# Revit family: RRPOSTM
name_source: partatom
category: Generic Models
revit_build: Autodesk Revit 2018 (Build: 20190510_1515(x64)
units: mm (PartAtom-declared; Revit-internal decimal feet)

## family parameters
Always vertical = No
Can host rebar = No
Cut with Voids When Loaded = No
Part Type = Normal
Room Calculation Point = No
Round Connector Dimension = Use Diameter
Shared = Yes
Work Plane-Based = Yes

## types (8) — shared parameters
Cap Height = 1.5 "
Default Elevation = 48 "
Diameter = 2.38 "
Patent Information = 10495237, 10,697,562, 10,844,978, 11,262,000

## per-type parameters (varying)
| type | Description | Height | Post Height |
| RRPOSTM30496 | One Post Mount 2 Inch Schedule 40 Pipe  304 96 Inch High | 96 " | 94.25 " |
| RRPOSTM30448 | One Post Mount 2 Inch Schedule 40 Pipe  304 48 Inch High | 48 " | 46.25 " |
| RRPOSTM30460 | One Post Mount 2 Inch Schedule 40 Pipe  304 60 Inch High | 60 " | 58.25 " |
| RRPOSTM30472 | One Post Mount 2 Inch Schedule 40 Pipe  304 72 Inch High | 72 " | 70.25 " |
| RRPOSTM30478 | One Post Mount 2 Inch Schedule 40 Pipe  304 78 Inch High | 78 " | 76.25 " |
| RRPOSTM30484 | One Post Mount 2 Inch Schedule 40 Pipe  304 84 Inch High | 84 " | 82.25 " |
| RRPOSTM304108 | One Post Mount 2 Inch Schedule 40 Pipe  304 108 Inch High | 108 " | 106.25 " |
| RRPOSTM304120 | One Post Mount 2 Inch Schedule 40 Pipe  304 120 Inch High | 120 " | 118.25 " |

note: column(s) folded — value = type name in every type: Catalog Number

## geometry (parser evidence)
native form markers: Sweep x10
no freeform markers — native parametric forms only
